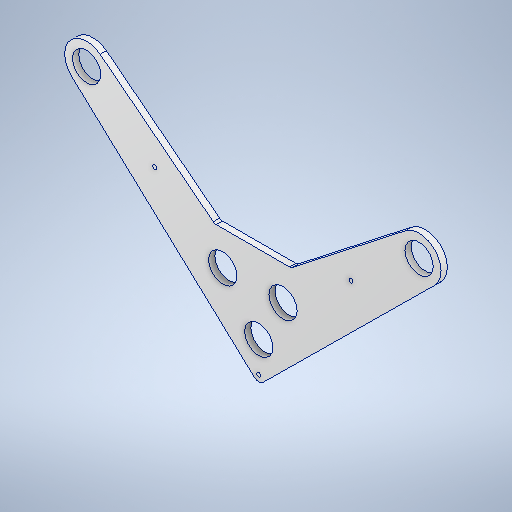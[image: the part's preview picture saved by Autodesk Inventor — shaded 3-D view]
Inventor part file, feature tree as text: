
AUTODESK INVENTOR PART (.ipt)
format: ipt  version: 2025.1 (Build 291241020, 241B)  size: 332,800 bytes
history: native  units: in
note: dims shown in document units (in); Inventor stores cm internally (conversion verified against a paired STEP export)
features: extrude x1, sketch x1
ambient origin geometry x8: Origin, YZ Plane, XZ Plane, XY Plane, X Axis, Y Axis, Z Axis, Center Point
bodies: Solid1 (feature_tree)
feature tree (2):
  extrude  "Extrusion1"  Depth=0.25in
  sketch  "Sketch1"  dims[d0=1.6in d3=0.1in d9=2.4in d10=0.1in d12=0.063in d13=1.125in d14=1.504in d15=1.654in d16=6.879in d17=0.7146in d18=1.125in d24=1.75in d25=1.75in d37=0.188in d38=0.063in d39=0.159in d40=0.5in d41=0.159in d42=0.063in d43=0.5in d44=0.5in d45=0.159in d46=3.4395in d47=3.4395in d48=4.0in d49=4.0in d50=0.25in d51=0.0in]
